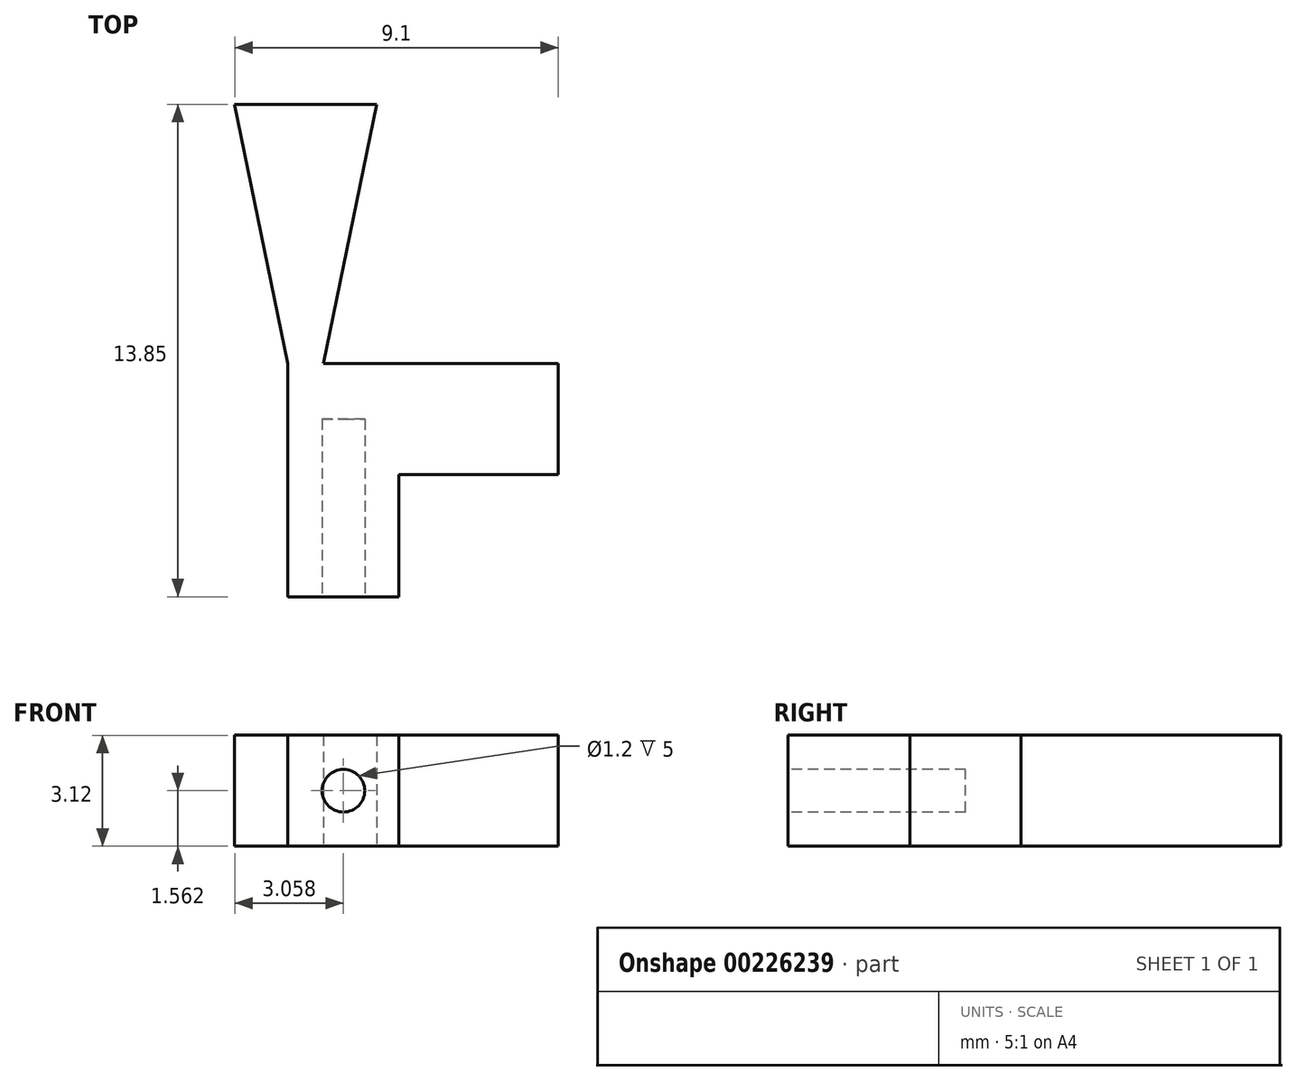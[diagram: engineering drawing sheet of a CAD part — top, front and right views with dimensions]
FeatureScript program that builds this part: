
annotation { "Feature Type Name" : "Feature", "Feature Type Description" : "" }
export const myFeature = defineFeature(function(context is Context, id is Id, definition is map)
    precondition{}
    {
        {
            var Q0;
            Q0=qCreatedBy(makeId("Top.planeOp"),FACE);
            var sketch = newSketch(context, id + "F0", { "sketchPlane" : qUnion([Q0])});
            skLineSegment(sketch, "E0.bottom", {"start": v(0, 0) * mm, "end": v(20.83, 0) * mm, "construction": true});
            skLineSegment(sketch, "E0.top", {"start": v(0, 20.83) * mm, "end": v(20.83, 20.83) * mm, "construction": true});
            skLineSegment(sketch, "E0.left", {"start": v(0, 0) * mm, "end": v(0, 20.83) * mm, "construction": true});
            skLineSegment(sketch, "E0.right", {"start": v(20.83, 0) * mm, "end": v(20.83, 20.83) * mm, "construction": true});
            skPoint(sketch, "E1.centerSnap0", {"position": v(0, 10.42) * mm});
            skLineSegment(sketch, "E2", {"start": v(10.42, 20.83) * mm, "end": v(10.42, 0) * mm, "construction": true});
            skLineSegment(sketch, "E3.bottom", {"start": v(1.56, 20.83) * mm, "end": v(19.27, 20.83) * mm, "construction": true});
            skLineSegment(sketch, "E3.top", {"start": v(1.56, 0) * mm, "end": v(19.27, 0) * mm, "construction": true});
            skLineSegment(sketch, "E3.left", {"start": v(1.56, 20.83) * mm, "end": v(1.56, 0) * mm, "construction": true});
            skLineSegment(sketch, "E3.right", {"start": v(19.27, 20.83) * mm, "end": v(19.27, 0) * mm, "construction": true});
            skPoint(sketch, "E3.middle", {"position": v(10.42, 10.42) * mm});
            skCircle(sketch, "E4", {"center": v(-6.04, 10.42) * mm, "radius": 7.6 * mm, "construction": true});
            skLineSegment(sketch, "E5", {"start": v(-7.6, 0) * mm, "end": v(-4.48, 0) * mm});
            skLineSegment(sketch, "E6", {"start": v(-4.48, 0) * mm, "end": v(-4.48, 3.44) * mm});
            skLineSegment(sketch, "E7", {"start": v(-4.48, 3.44) * mm, "end": v(0, 3.44) * mm});
            skLineSegment(sketch, "E8", {"start": v(0, 3.44) * mm, "end": v(0, 6.56) * mm});
            skLineSegment(sketch, "E9", {"start": v(0, 6.56) * mm, "end": v(-7.6, 6.56) * mm});
            skLineSegment(sketch, "E10", {"start": v(-7.6, 6.56) * mm, "end": v(-7.6, 0) * mm});
            skLineSegment(sketch, "E11", {"start": v(-6.04, 10.42) * mm, "end": v(-6.04, 0) * mm, "construction": true});
            skPoint(sketch, "E11.endSnap0", {"position": v(-6.04, 0) * mm});
            skLineSegment(sketch, "E12", {"start": v(-6.6, 6.56) * mm, "end": v(-5.1, 13.85) * mm});
            skLineSegment(sketch, "E13", {"start": v(-5.1, 13.85) * mm, "end": v(-9.1, 13.85) * mm});
            skLineSegment(sketch, "E14", {"start": v(-9.1, 13.85) * mm, "end": v(-7.6, 6.56) * mm});
            skSolve(sketch);
        }
        {
            var Q0;
            Q0 = qSketchRegion(id + "F0", true);
            extrude(context, id + "F1", {"entities" : qUnion([Q0]), "depth" : 150 / 48 * mm});
        }
        {
            var Q0;
            Q0=makeQuery(id+"F1.opExtrude","SWEPT_FACE",FACE,{"disambiguationData":[OSD([sQuery(id+"F0.wireOp",EDGE,"E5")])]});
            var sketch = newSketch(context, id + "F2", { "sketchPlane" : qUnion([Q0])});
            skLineSegment(sketch, "E15", {"start": v(-7.6, 3.13) * mm, "end": v(-4.48, 0) * mm, "construction": true});
            skPoint(sketch, "E16", {"position": v(-6.04, 1.56) * mm});
            skCircle(sketch, "E17", {"center": v(-6.04, 1.56) * mm, "radius": 0.6 * mm});
            skSolve(sketch);
        }
        {
            var Q0;
            Q0 = qSketchRegion(id + "F2", true);
            extrude(context, id + "F3", {"entities" : qUnion([Q0]), "operationType" : NewBodyOperationType.REMOVE, "oppositeDirection" : true, "depth" : 5 * mm});
        }
    });
